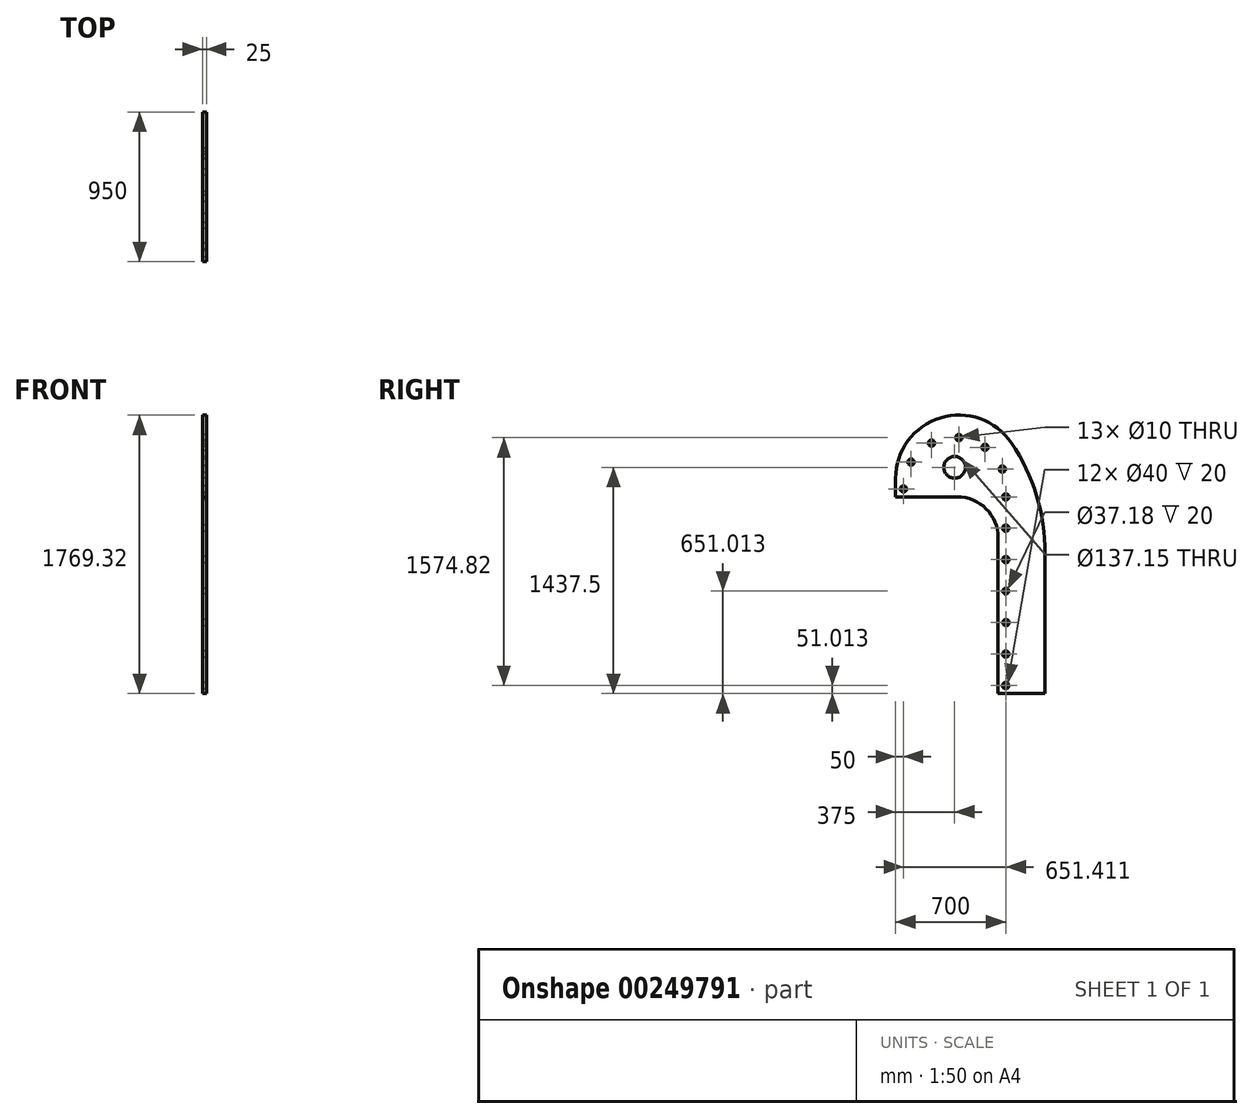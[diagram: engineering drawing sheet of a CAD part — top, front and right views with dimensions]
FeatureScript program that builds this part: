
annotation { "Feature Type Name" : "Feature", "Feature Type Description" : "" }
export const myFeature = defineFeature(function(context is Context, id is Id, definition is map)
    precondition{}
    {
        {
            var Q0;
            Q0=qCreatedBy(makeId("Right.planeOp"),FACE);
            var sketch = newSketch(context, id + "F0", { "sketchPlane" : qUnion([Q0])});
            skLineSegment(sketch, "E0.bottom", {"start": v(0, 0) * mm, "end": v(-298.59, 0) * mm});
            skLineSegment(sketch, "E0.left", {"start": v(0, 0) * mm, "end": v(0, 892.05) * mm});
            skPoint(sketch, "E1.startSnap0", {"position": v(-575, 1625) * mm});
            skCircle(sketch, "E2.0.1.0", {"center": v(-250, 1051.01) * mm, "radius": 20 * mm});
            skCircle(sketch, "E2.0.2.0", {"center": v(-250, 851.01) * mm, "radius": 20 * mm});
            skCircle(sketch, "E2.0.3.0", {"center": v(-250, 651.01) * mm, "radius": 18.59 * mm});
            skCircle(sketch, "E2.0.4.0", {"center": v(-248.59, 451.01) * mm, "radius": 20 * mm});
            skCircle(sketch, "E2.0.5.0", {"center": v(-250, 251.01) * mm, "radius": 20 * mm});
            skCircle(sketch, "E2.0.6.0", {"center": v(-250.61, 51.01) * mm, "radius": 20 * mm});
            skCircle(sketch, "E3", {"center": v(-900, 1300) * mm, "radius": 20 * mm});
            skCircle(sketch, "E4.1.0", {"center": v(-851.88, 1470.6) * mm, "radius": 20 * mm});
            skCircle(sketch, "E4.2.0", {"center": v(-721.8, 1591) * mm, "radius": 20 * mm});
            skCircle(sketch, "E4.3.0", {"center": v(-548.01, 1625.83) * mm, "radius": 20 * mm});
            skCircle(sketch, "E4.4.0", {"center": v(-381.59, 1564.83) * mm, "radius": 20 * mm});
            skCircle(sketch, "E4.5.0", {"center": v(-271.46, 1425.95) * mm, "radius": 20 * mm});
            skCircle(sketch, "E4.6.0", {"center": v(-250, 1250) * mm, "radius": 20 * mm});
            skPoint(sketch, "E4.center", {"position": v(-573.09, 1299.88) * mm});
            skArc(sketch, "E5", {"start": v(-213.75, 1591.76) * mm, "mid": v(-665.11, 1751.76) * mm, "end": v(-950, 1366.85) * mm});
            skLineSegment(sketch, "E6.top", {"start": v(-850, 1250) * mm, "end": v(-950, 1250) * mm});
            skLineSegment(sketch, "E6.right", {"start": v(-950, 1253.18) * mm, "end": v(-950, 1250) * mm});
            skPoint(sketch, "E7.newPointA", {"position": v(-306.34, 1250) * mm});
            skLineSegment(sketch, "E8.trimOffspring", {"start": v(-558.7, 1250) * mm, "end": v(-850, 1250) * mm});
            skPoint(sketch, "E0.top.end.orphan", {"position": v(-256.34, 1089) * mm});
            skCircle(sketch, "E9", {"center": v(-575, 1437.5) * mm, "radius": 68.58 * mm});
            skLineSegment(sketch, "E10.trimOffspring", {"start": v(-298.59, 989.89) * mm, "end": v(-298.59, 0) * mm});
            skArc(sketch, "E11", {"start": v(-558.7, 1250) * mm, "mid": v(-374.77, 1173.82) * mm, "end": v(-298.59, 989.89) * mm});
            skArc(sketch, "E12.0", {"start": v(-213.75, 1591.76) * mm, "mid": v(-54.63, 1257.87) * mm, "end": v(0, 892.05) * mm});
            skCircle(sketch, "E13", {"center": v(-721.8, 1591) * mm, "radius": 5 * mm});
            skCircle(sketch, "E14", {"center": v(-548.01, 1625.83) * mm, "radius": 5 * mm});
            skCircle(sketch, "E15", {"center": v(-851.88, 1470.6) * mm, "radius": 5 * mm});
            skCircle(sketch, "E16", {"center": v(-900, 1300) * mm, "radius": 5 * mm});
            skCircle(sketch, "E17", {"center": v(-381.59, 1564.83) * mm, "radius": 5 * mm});
            skCircle(sketch, "E18", {"center": v(-271.46, 1425.95) * mm, "radius": 5 * mm});
            skCircle(sketch, "E19", {"center": v(-250, 1250) * mm, "radius": 5 * mm});
            skCircle(sketch, "E20", {"center": v(-250, 1051.01) * mm, "radius": 5 * mm});
            skCircle(sketch, "E21", {"center": v(-250, 851.01) * mm, "radius": 5 * mm});
            skCircle(sketch, "E22", {"center": v(-250, 651.01) * mm, "radius": 5 * mm});
            skCircle(sketch, "E23", {"center": v(-248.59, 451.01) * mm, "radius": 5 * mm});
            skCircle(sketch, "E24", {"center": v(-250, 251.01) * mm, "radius": 5 * mm});
            skCircle(sketch, "E25", {"center": v(-250.61, 51.01) * mm, "radius": 5 * mm});
            skLineSegment(sketch, "E26", {"start": v(-270, 1250) * mm, "end": v(-230, 1250) * mm, "construction": true});
            skPoint(sketch, "E27.orphan", {"position": v(-53.97, 1250) * mm});
            skLineSegment(sketch, "E28", {"start": v(-950, 1366.85) * mm, "end": v(-950, 1250) * mm});
            skSolve(sketch);
        }
        {
            var Q0;
            Q0=makeQuery(id+"F0.imprint","IMPRINT",FACE,{"disambiguationData":[TD([[makeQuery(id+"F0.imprint","IMPRINT",EDGE,{"derivedFrom":sQuery(id+"F0.wireOp",EDGE,"E0.bottom")}),-1.0]])]});
            extrude(context, id + "F1", {"entities" : qUnion([Q0]), "depth" : 25 * mm});
        }
        {
            var Q0;
            Q0=makeQuery(id+"F0.imprint","IMPRINT",FACE,{"disambiguationData":[TD([[makeQuery(id+"F0.imprint","IMPRINT",EDGE,{"derivedFrom":sQuery(id+"F0.wireOp",EDGE,"E2.0.6.0")}),1.0]])]});
            var Q1;
            Q1=makeQuery(id+"F0.imprint","IMPRINT",FACE,{"disambiguationData":[TD([[makeQuery(id+"F0.imprint","IMPRINT",EDGE,{"derivedFrom":sQuery(id+"F0.wireOp",EDGE,"E2.0.5.0")}),1.0]])]});
            var Q2;
            Q2=makeQuery(id+"F0.imprint","IMPRINT",FACE,{"disambiguationData":[TD([[makeQuery(id+"F0.imprint","IMPRINT",EDGE,{"derivedFrom":sQuery(id+"F0.wireOp",EDGE,"E2.0.4.0")}),1.0]])]});
            var Q3;
            Q3=makeQuery(id+"F0.imprint","IMPRINT",FACE,{"disambiguationData":[TD([[makeQuery(id+"F0.imprint","IMPRINT",EDGE,{"derivedFrom":sQuery(id+"F0.wireOp",EDGE,"E2.0.3.0")}),1.0]])]});
            var Q4;
            Q4=makeQuery(id+"F0.imprint","IMPRINT",FACE,{"disambiguationData":[TD([[makeQuery(id+"F0.imprint","IMPRINT",EDGE,{"derivedFrom":sQuery(id+"F0.wireOp",EDGE,"E2.0.2.0")}),1.0]])]});
            var Q5;
            Q5=makeQuery(id+"F0.imprint","IMPRINT",FACE,{"disambiguationData":[TD([[makeQuery(id+"F0.imprint","IMPRINT",EDGE,{"derivedFrom":sQuery(id+"F0.wireOp",EDGE,"E2.0.1.0")}),1.0]])]});
            var Q6;
            Q6=makeQuery(id+"F0.imprint","IMPRINT",FACE,{"disambiguationData":[TD([[makeQuery(id+"F0.imprint","IMPRINT",EDGE,{"derivedFrom":sQuery(id+"F0.wireOp",EDGE,"E4.6.0")}),1.0]])]});
            var Q7;
            Q7=makeQuery(id+"F0.imprint","IMPRINT",FACE,{"disambiguationData":[TD([[makeQuery(id+"F0.imprint","IMPRINT",EDGE,{"derivedFrom":sQuery(id+"F0.wireOp",EDGE,"E4.5.0")}),1.0]])]});
            var Q8;
            Q8=makeQuery(id+"F0.imprint","IMPRINT",FACE,{"disambiguationData":[TD([[makeQuery(id+"F0.imprint","IMPRINT",EDGE,{"derivedFrom":sQuery(id+"F0.wireOp",EDGE,"E4.4.0")}),1.0]])]});
            var Q9;
            Q9=makeQuery(id+"F0.imprint","IMPRINT",FACE,{"disambiguationData":[TD([[makeQuery(id+"F0.imprint","IMPRINT",EDGE,{"derivedFrom":sQuery(id+"F0.wireOp",EDGE,"E4.3.0")}),1.0]])]});
            var Q10;
            Q10=makeQuery(id+"F0.imprint","IMPRINT",FACE,{"disambiguationData":[TD([[makeQuery(id+"F0.imprint","IMPRINT",EDGE,{"derivedFrom":sQuery(id+"F0.wireOp",EDGE,"E4.2.0")}),1.0]])]});
            var Q11;
            Q11=makeQuery(id+"F0.imprint","IMPRINT",FACE,{"disambiguationData":[TD([[makeQuery(id+"F0.imprint","IMPRINT",EDGE,{"derivedFrom":sQuery(id+"F0.wireOp",EDGE,"E4.1.0")}),1.0]])]});
            var Q12;
            Q12=makeQuery(id+"F0.imprint","IMPRINT",FACE,{"disambiguationData":[TD([[makeQuery(id+"F0.imprint","IMPRINT",EDGE,{"derivedFrom":sQuery(id+"F0.wireOp",EDGE,"E3")}),1.0]])]});
            extrude(context, id + "F2", {"entities" : qUnion([Q0, Q1, Q2, Q3, Q4, Q5, Q6, Q7, Q8, Q9, Q10, Q11, Q12]), "operationType" : NewBodyOperationType.ADD, "depth" : 5 * mm});
        }
    });
